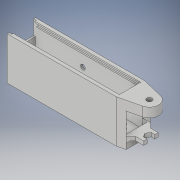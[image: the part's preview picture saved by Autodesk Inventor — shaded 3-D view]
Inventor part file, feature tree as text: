
AUTODESK INVENTOR PART (.ipt)
format: ipt  version: 2019 (Build 230136000, 136)  size: 669,184 bytes
history: native  units: mm
features: sketch x18, extrude x16, plane x2, chamfer x2, sweep x1, shell x1, hole x1, mirror x1, projected_geometry x1
ambient origin geometry x8: Origin, YZ Plane, XZ Plane, XY Plane, X Axis, Y Axis, Z Axis, Center Point
bodies: Body1 (feature_tree)
feature tree (43):
  sweep  "Sweep1"
  shell  "Shell1"  Thickness=15.0mm
  hole  "Hole4"  [1 undecoded]
  extrude  "Extrusion4"  Depth=25.0mm
  extrude  "Extrusion5"  Depth=88.0mm
  plane  "Work Plane4"
  extrude  "Extrusion6"  Depth=8.0mm
  extrude  "Extrusion7"  Depth=10.0mm TaperAngle=0.0deg
  extrude  "Extrusion12"  Depth=22.7mm
  extrude  "Extrusion11"  Depth=10.0mm TaperAngle=0.0deg
  extrude  "Extrusion10"  Depth=4.0mm TaperAngle=0.0deg
  plane  "Work Plane5"
  extrude  "Extrusion15"  Depth=8.0mm
  mirror  "Mirror1"
  extrude  "Extrusion16"  Depth=4.0mm TaperAngle=0.0deg
  extrude  "Extrusion19"  Depth=12.0mm
  extrude  "Extrusion24"  Depth=1.5mm
  extrude  "Extrusion25"  Depth=1.5mm
  extrude  "Extrusion26"  Depth=1.5mm
  extrude  "Extrusion27"  Depth=15.0mm
  chamfer  "Chamfer1"  Distance=1.5mm
  chamfer  "Chamfer2"  Distance=3.0mm
  extrude  "Extrusion28"  Depth=3.0mm
  extrude  "Extrusion29"  Depth=1.5mm TaperAngle=0.0deg
  sketch  "Sketch5"  dims[d25=42.0mm d28=0.0mm d29=0.0mm d52=15.0mm]
  sketch  "Sketch6"  dims[d53=20.0mm d54=5.5mm]
  sketch  "Sketch12"  dims[d55=110.0mm d56=25.0mm]
  sketch  "Sketch14"  dims[d57=2.0mm d58=88.0mm]
  sketch  "Sketch15"  dims[d59=10.0mm]
  sketch  "Sketch16"  dims[d60=5.5mm d61=6.0mm d62=15.0mm d63=4.3mm d64=90.0deg d65=8.0mm d66=20.594885mm d67=5.5mm]
  sketch  "Sketch17"  dims[d68=19.0mm d69=10.0mm d70=0.0mm]
  sketch  "Sketch20"  dims[d71=10.0mm d72=0.0mm d73=22.7mm]
  sketch  "Sketch21"  dims[d74=25.0mm d75=10.0mm d76=0.0mm]
  sketch  "Sketch22"  dims[d77=8.0mm d78=4.0mm d79=0.0mm]
  sketch  "Sketch25"  dims[d90=2.0mm d91=0.0mm d92=8.0mm]
  projected_geometry  "Projected Loop1"
  sketch  "Sketch29"  dims[d93=8.0mm d94=4.0mm d95=0.0mm]
  sketch  "Sketch36"  dims[d96=12.0mm d97=12.0mm]
  sketch  "Sketch37"  dims[d98=4.0mm d99=0.0mm d105=1.5mm]
  sketch  "Sketch38"  dims[d106=1.5mm d107=1.5mm]
  sketch  "Sketch39"  dims[d108=1.5mm d109=0.0mm d110=1.5mm]
  sketch  "Sketch40"  dims[d111=1.5mm d112=15.0mm d113=1.5mm d114=0.0mm]
  sketch  "Sketch41"  dims[d123=3.0mm d125=3.0mm d127=3.0mm d128=1.5mm d129=0.0mm d132=45.0deg d133=45.0deg d134=2.0mm d136=7.0mm d138=0.75mm d139=0.75mm d149=10.0mm d150=0.0mm d151=2.0mm d152=10.0mm d153=0.0mm d154=15.0mm d155=13.0mm d156=0.0mm d157=4.0mm d158=8.0mm d159=15.0mm d160=0.0mm d161=5.0mm d162=2.0mm d163=45.0deg d164=2.0mm d165=2.0mm d166=45.0deg d167=8.55mm d168=0.1mm d169=0.0mm d172=10.0mm d173=0.0mm d176=51.0mm d177=5.0mm d179=17.65mm d38=1.0mm d39=1.0mm d40=8.0mm d41=0.15mm d42=3.4mm d43=0.375mm d44=14.3117mm d45=0.75mm d46=20.594885mm d47=0.0625mm d48=0.75mm d49=0.375mm]
note: 1 required parameter value undecoded (feature->parameter linkage not recoverable at this tier; creation-order binding heuristic only, values carry confidence <= 0.55)
